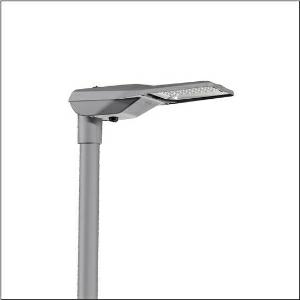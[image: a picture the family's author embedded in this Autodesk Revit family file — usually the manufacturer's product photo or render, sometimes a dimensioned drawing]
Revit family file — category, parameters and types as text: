
# Revit family: streetlight_sl_21_iq_mini___p0_8ab_5xe2r31y08gb_b9a0
name_source: partatom
category: Lighting Fixtures
units: mm (PartAtom-declared; Revit-internal decimal feet)

## family parameters
Cut with Voids When Loaded = No
Host = Face
Light Source = No
Part Type = Normal
Room Calculation Point = No
Round Connector Dimension = Use Diameter
Shared = No

## types (1)
- --- (1 x LED, 5200 lm, 39.8 W, 3000K)
    Apparent Load = 40 VA
    CIE Flux Codes = 36 71 98 100 100
    Color Rendering = 70
    Color Temperature = 3000K
    Default Elevation = 1800 mm
    Description = Streetlight SL 21 iQ mini, mast luminaire, primary light control with lens, of PMMA, primary optical cover: cover, of toughened safety glass, transparent, light distribution: P0.8aB, light emission: direct distribution, primary light characteristic: asymmetric, installation type: post-top, side-entry, LED, High Power LED, rated luminous flux: 5.200lm, luminous efficacy: 131lm/W, light colour: 730, colour temperature: 3000K, control gear: iQ-Street Remote, D4i with power reduction, control: pre-setting: logarithmic dimming characteristic, Street-Remote, Auto-Match, Temp-Guard, Lumen-Switch, Night-Set, Smart-Wire, Light-Fading, Desk-Remote (wireless, voltage-free reading and setting of iQ features in the workshop via application-optimized NFC function/RFID function), optimised constant luminous flux control (CLO 2.0), mains connection: 220..240V, AC, 50/60Hz, start of lifetime: 40W, end of service life: 41W, reduction: 18W, luminaire housing, of diecast aluminium, powder-coated, Siteco® metallic grey (DB 702S), corrosivity category C5 mid according to DIN EN ISO 12944, please order mast flange separately, inclination adjustable: 0°, 5°, 10°, 15°, sealing non-destructively replaceable, multi-level sealing system, length: 628mm, width: 235mm, height: 110mm, mast flange for spigot size: 42mm (side-entry): 5XC10008XM4, 60/48mm (side-entry/post-top): 5XC10108XM2, 76/60mm (side-entry/post-top): 5XC10108XM1, mounting height: 4..8m, Smart Interface below and above, protection rating (complete): IP66, insulation class (complete): insulation class II (safety insulation), certification: CE, ENEC, ENEC+, VDE, impact resistance: IK10, permissible operating ambient temperature for outdoor applications: -40..+50°C, standard-compliant lighting for roads and squares, packaging unit: 1 piece

Light Distribution: P0.8aB
    Height = 110 mm
    Lamp = 1 x LED
    Lamp Light Flux = 5200 lm
    Lamp Power = 39.8 W
    Lamp count = 1
    Length = 625 mm
    Luminous efficacy = 131 lm/W
    Manufacturer = Siteco
    ModVariant = No
    Model = 5XE2R31Y08GB
    Number of Poles = 1
    OnlyDefault = Yes
    Power Factor = 1
    Product Name = Streetlight SL 21 iQ mini | P0.8aB
    Product group = mast luminaire | pylon top
    ProductGroupID = 6100
    Protection Class = Protection class II
    Protection Degree = IP 66
    RLX_Detail_Level = 1
    RLX_Emergency_Light_Flux = 0 lm
    RLX_Emergency_Type = 0
    RLX_Emergency_Type_DB = No
    RlxData = <blob elided: 26497 chars, md5=092bdea6>
    Socket = socket
    Standby Power = 0 W
    System Light Flux = 5200 lm
    System Power = 40 W
    Type Comments = factory setting: luminous flux: 100 % | dim-lin: 254 | 800 mA
    Type Image = l_1003514.jpg
    URL = http://relux.com
    VarID = @adj_075348
    Voltage = 0 V
    Weight = 0.00 kg
    Width = 234 mm

## geometry (parser evidence)
native form markers: Blend x4, Sweep x11
no freeform markers — native parametric forms only
